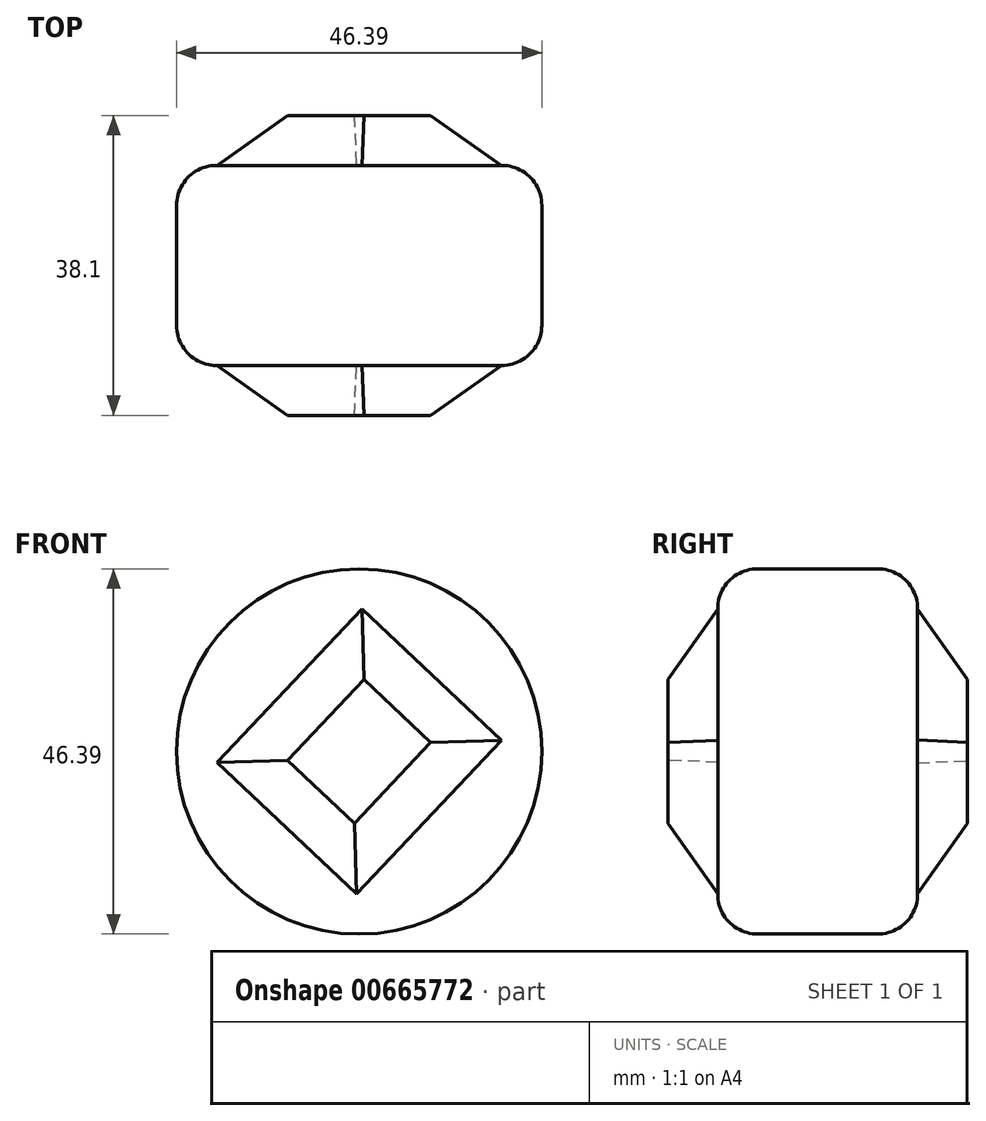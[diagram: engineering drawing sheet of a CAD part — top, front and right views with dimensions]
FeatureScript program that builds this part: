
annotation { "Feature Type Name" : "Feature", "Feature Type Description" : "" }
export const myFeature = defineFeature(function(context is Context, id is Id, definition is map)
    precondition{}
    {
        {
            var Q0;
            Q0=qCreatedBy(makeId("Front.planeOp"),FACE);
            var sketch = newSketch(context, id + "F0", { "sketchPlane" : qUnion([Q0])});
            skCircle(sketch, "E0", {"center": v(-16.93, -16.93) * mm, "radius": 23.2 * mm});
            skSolve(sketch);
        }
        {
            var Q0;
            Q0=makeQuery(id+"F0.imprint","IMPRINT",FACE,{"disambiguationData":[TD([[makeQuery(id+"F0.imprint","IMPRINT",EDGE,{"derivedFrom":sQuery(id+"F0.wireOp",EDGE,"E0")}),1.0]])]});
            extrude(context, id + "F1", {"entities" : qUnion([Q0]), "depth" : 12.7 * mm, "offsetDistance" : 25.4 * mm});
        }
        {
            var Q0;
            Q0=makeQuery(id+"F1.opExtrude","CAP_FACE",FACE,{"disambiguationData":[OSD([sQuery(id+"F0.wireOp",EDGE,"E0")])],"isStart":true});
            var sketch = newSketch(context, id + "F2", { "sketchPlane" : qUnion([Q0])});
            skSolve(sketch);
        }
        {
            var Q0;
            Q0=qSketchRegion(id+"F2",true);
            var Q1;
            Q1=makeQuery(id+"F2.imprint","IMPRINT",FACE,{"disambiguationData":[TD([[makeQuery(id+"F2.imprint","IMPRINT",EDGE,{"derivedFrom":makeQuery(id+"F1.opExtrude","CAP_EDGE",EDGE,{"disambiguationData":[OSD([sQuery(id+"F0.wireOp",EDGE,"E0")])],"isStart":true})}),-1.0]])]});
            extrude(context, id + "F3", {"entities" : qUnion([Q0, Q1]), "operationType" : NewBodyOperationType.ADD, "depth" : 12.7 * mm, "offsetDistance" : 25.4 * mm});
        }
        {
            var Q0;
            Q0=makeQuery(id+"F3.opExtrude","CAP_FACE",FACE,{"disambiguationData":[OSD([sQuery(id+"F0.wireOp",EDGE,"E0")])],"isStart":false});
            var Q1;
            {var subQ0=sQuery(id+"F0.wireOp",EDGE,"E0");Q1=makeQuery(id+"F3.boolean.opBoolean","MERGE",FACE,{"derivedFrom":[makeQuery(id+"F1.opExtrude","SWEPT_FACE",FACE,{"disambiguationData":[OSD([subQ0])]}),makeQuery(id+"F3.opExtrude","SWEPT_FACE",FACE,{"disambiguationData":[OSD([subQ0])]})]});}
            var Q2;
            Q2=makeQuery(id+"F1.opExtrude","CAP_EDGE",EDGE,{"disambiguationData":[OSD([sQuery(id+"F0.wireOp",EDGE,"E0")])],"isStart":false});
            var Q3;
            Q3=makeQuery(id+"F3.opExtrude","CAP_EDGE",EDGE,{"disambiguationData":[OSD([sQuery(id+"F0.wireOp",EDGE,"E0")])],"isStart":false});
            var Q4;
            Q4=makeQuery(id+"F1.opExtrude","CAP_FACE",FACE,{"disambiguationData":[OSD([sQuery(id+"F0.wireOp",EDGE,"E0")])],"isStart":false});
            fillet(context, id + "F4", {"entities" : qUnion([Q0, Q1, Q2, Q3, Q4]), "radius" : 5.08 * mm, "tangentPropagation" : true, "allowEdgeOverflow" : false});
        }
        {
            var Q0;
            Q0=makeQuery(id+"F3.opExtrude","CAP_FACE",FACE,{"disambiguationData":[OSD([sQuery(id+"F0.wireOp",EDGE,"E0")])],"isStart":false});
            var sketch = newSketch(context, id + "F5", { "sketchPlane" : qUnion([Q0])});
            skLineSegment(sketch, "E1", {"start": v(16.57, 1.2) * mm, "end": v(34.99, -18.36) * mm});
            skLineSegment(sketch, "E2", {"start": v(34.99, -18.36) * mm, "end": v(17.28, -35.04) * mm});
            skLineSegment(sketch, "E3", {"start": v(17.28, -35.04) * mm, "end": v(-1.14, -15.49) * mm});
            skLineSegment(sketch, "E4", {"start": v(-1.14, -15.49) * mm, "end": v(16.57, 1.2) * mm});
            skSolve(sketch);
        }
        {
            var Q0;
            Q0=makeQuery(id+"F1.opExtrude","CAP_FACE",FACE,{"disambiguationData":[OSD([sQuery(id+"F0.wireOp",EDGE,"E0")])],"isStart":false});
            var sketch = newSketch(context, id + "F6", { "sketchPlane" : qUnion([Q0])});
            skLineSegment(sketch, "E5", {"start": v(-16.59, 1.2) * mm, "end": v(1.14, -15.54) * mm});
            skLineSegment(sketch, "E6", {"start": v(1.14, -15.54) * mm, "end": v(-17.26, -35.04) * mm});
            skLineSegment(sketch, "E7", {"start": v(-17.26, -35.04) * mm, "end": v(-35, -18.3) * mm});
            skLineSegment(sketch, "E8", {"start": v(-35, -18.3) * mm, "end": v(-16.59, 1.2) * mm});
            skSolve(sketch);
        }
        {
            var Q0;
            Q0=makeQuery(id+"F5.imprint","IMPRINT",FACE,{"disambiguationData":[TD([[makeQuery(id+"F5.imprint","IMPRINT",EDGE,{"derivedFrom":sQuery(id+"F5.wireOp",EDGE,"E1")}),-1.0]])]});
            extrude(context, id + "F7", {"entities" : qUnion([Q0]), "operationType" : NewBodyOperationType.ADD, "depth" : 6.35 * mm, "offsetDistance" : 25.4 * mm});
        }
        {
            var Q0;
            Q0=makeQuery(id+"F6.imprint","IMPRINT",FACE,{"disambiguationData":[TD([[makeQuery(id+"F6.imprint","IMPRINT",EDGE,{"derivedFrom":sQuery(id+"F6.wireOp",EDGE,"E5")}),-1.0]])]});
            extrude(context, id + "F8", {"entities" : qUnion([Q0]), "operationType" : NewBodyOperationType.ADD, "depth" : 6.35 * mm, "offsetDistance" : 25.4 * mm});
        }
        {
            var Q0;
            Q0=makeQuery(id+"F7.opExtrude","CAP_FACE",FACE,{"disambiguationData":[OSD([sQuery(id+"F5.wireOp",EDGE,"E1"),sQuery(id+"F5.wireOp",EDGE,"E2"),sQuery(id+"F5.wireOp",EDGE,"E3"),sQuery(id+"F5.wireOp",EDGE,"E4")])],"isStart":false});
            chamfer(context, id + "F9", {"entities" : qUnion([Q0]), "width" : 6.35 * mm, "tangentPropagation" : true});
        }
        {
            var Q0;
            Q0=makeQuery(id+"F8.opExtrude","CAP_FACE",FACE,{"disambiguationData":[OSD([sQuery(id+"F6.wireOp",EDGE,"E5"),sQuery(id+"F6.wireOp",EDGE,"E6"),sQuery(id+"F6.wireOp",EDGE,"E7"),sQuery(id+"F6.wireOp",EDGE,"E8")])],"isStart":false});
            chamfer(context, id + "F10", {"entities" : qUnion([Q0]), "width" : 6.35 * mm, "tangentPropagation" : true});
        }
    });
